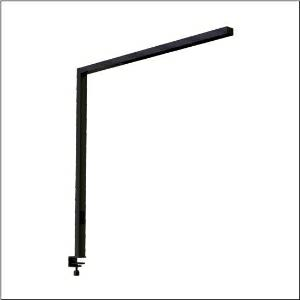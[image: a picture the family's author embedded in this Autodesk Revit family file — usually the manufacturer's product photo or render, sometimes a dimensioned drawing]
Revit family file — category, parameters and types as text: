
# Revit family: silica_r__31_desk_51my52gatcb_ad62
name_source: partatom
category: Lighting Fixtures
units: mm (PartAtom-declared; Revit-internal decimal feet)

## family parameters
Cut with Voids When Loaded = No
Host = Face
Light Source = No
Part Type = Normal
Room Calculation Point = No
Round Connector Dimension = Use Diameter
Shared = No

## types (1)
- --- (1 x LED, 8520 lm, 71 W, 4000K)
    Apparent Load = 71 VA
    CIE Flux Codes = 86 100 100 24 100
    Color Rendering = 80
    Color Temperature = 4000K
    Default Elevation = 1800 mm
    Description = Silica® 31 Desk, desktop luminaire, secondary optical cover: cover panel, of PMMA, light emission: direct/indirect distribution, primary light characteristic: symmetric, installation type: as desk luminaire, LED, rated luminous flux: 8.520lm, luminous efficacy: 120lm/W, light colour: 8tw, colour temperature: 2700..6500K, control gear: Touchdim, daylight-dependent control, with cable with plug, mains connection: 230V, AC, 50Hz, connection cable pre-assembled, rated input power: 71W, luminaire head, of aluminium, jet black (RAL 9005), length: 1.203mm, width: 52mm, supporting column, angular, of aluminium, jet black (RAL 9005), baseplate, of steel, jet black (RAL 9005), protection rating (complete): IP20, insulation class (complete): insulation class I (protective earthing), certification: CE, permissible operating ambient temperature: -20..+40°C, standard: EN 50419, packaging unit: 1 piece
    Height = 36 mm
    Lamp = 1 x LED
    Lamp Light Flux = 8520 lm
    Lamp Power = 71 W
    Lamp count = 1
    Length = 1203 mm
    Luminous efficacy = 120 lm/W
    Manufacturer = Siteco
    ModVariant = No
    Model = 51MY52GATCB
    Mounting Place = Floor
    Mounting Type = Freestanding
    Number of Poles = 1
    OnlyDefault = Yes
    Power Factor = 1
    Product Name = Silica® 31 Desk
    Product group = desktop luminaire
    ProductGroupID = 1303
    Protection Class = Protection class I
    Protection Degree = IP 20
    RLX_Detail_Level = 1
    RLX_Emergency_Light_Flux = 0 lm
    RLX_Emergency_Type = 0
    RLX_Emergency_Type_DB = No
    RlxData = <blob elided: 19137 chars, md5=06e66e92>
    Socket = socket
    Standby Power = 0 W
    System Light Flux = 8520 lm
    System Power = 71 W
    Type Comments = factory setting
    Type Image = l_1275329.jpg
    URL = http://relux.com
    VarID = @adj_080220
    Voltage = 0 V
    Weight = 0.00 kg
    Width = 52 mm  [stored 0.170604 ft]

note: [stored X ft] marks values corroborated as IEEE doubles in the binary element streams (Revit-internal decimal feet)

## geometry (parser evidence)
native form markers: Blend x4, Sweep x17
no freeform markers — native parametric forms only
